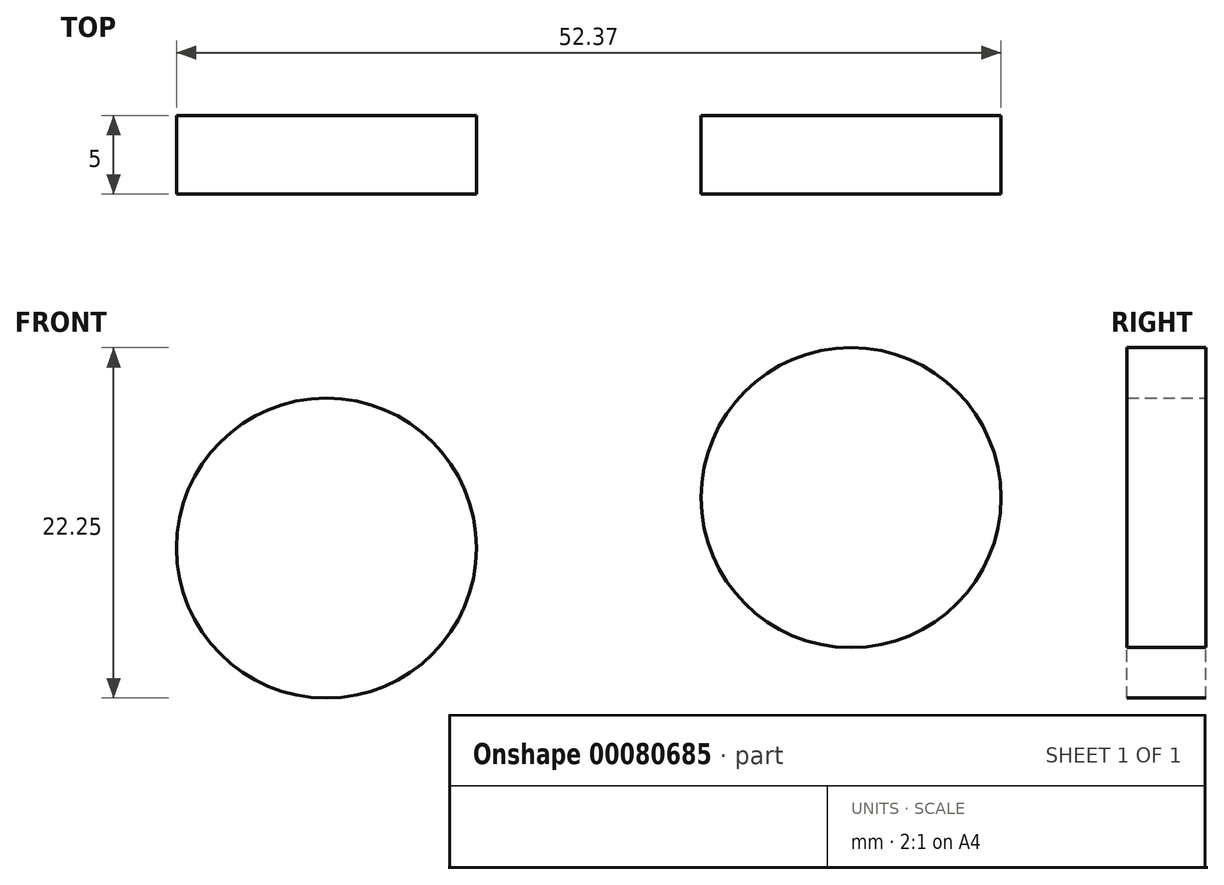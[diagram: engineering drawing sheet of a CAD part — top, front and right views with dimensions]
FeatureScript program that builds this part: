
annotation { "Feature Type Name" : "Feature", "Feature Type Description" : "" }
export const myFeature = defineFeature(function(context is Context, id is Id, definition is map)
    precondition{}
    {
        {
            var Q0;
            Q0=qCreatedBy(makeId("Front.planeOp"),FACE);
            var sketch = newSketch(context, id + "F0", { "sketchPlane" : qUnion([Q0])});
            skCircle(sketch, "E0", {"center": v(-49.19, 19.58) * mm, "radius": 9.53 * mm});
            skCircle(sketch, "E1", {"center": v(-15.87, 22.79) * mm, "radius": 9.53 * mm});
            skSolve(sketch);
        }
        {
            var Q0;
            Q0=makeQuery(id+"F0.imprint","IMPRINT",FACE,{"disambiguationData":[TD([[makeQuery(id+"F0.imprint","IMPRINT",EDGE,{"derivedFrom":sQuery(id+"F0.wireOp",EDGE,"E0")}),1.0]])]});
            var Q1;
            Q1=makeQuery(id+"F0.imprint","IMPRINT",FACE,{"disambiguationData":[TD([[makeQuery(id+"F0.imprint","IMPRINT",EDGE,{"derivedFrom":sQuery(id+"F0.wireOp",EDGE,"E1")}),1.0]])]});
            extrude(context, id + "F1", {"entities" : qUnion([Q0, Q1]), "depth" : 5 * mm});
        }
    });
